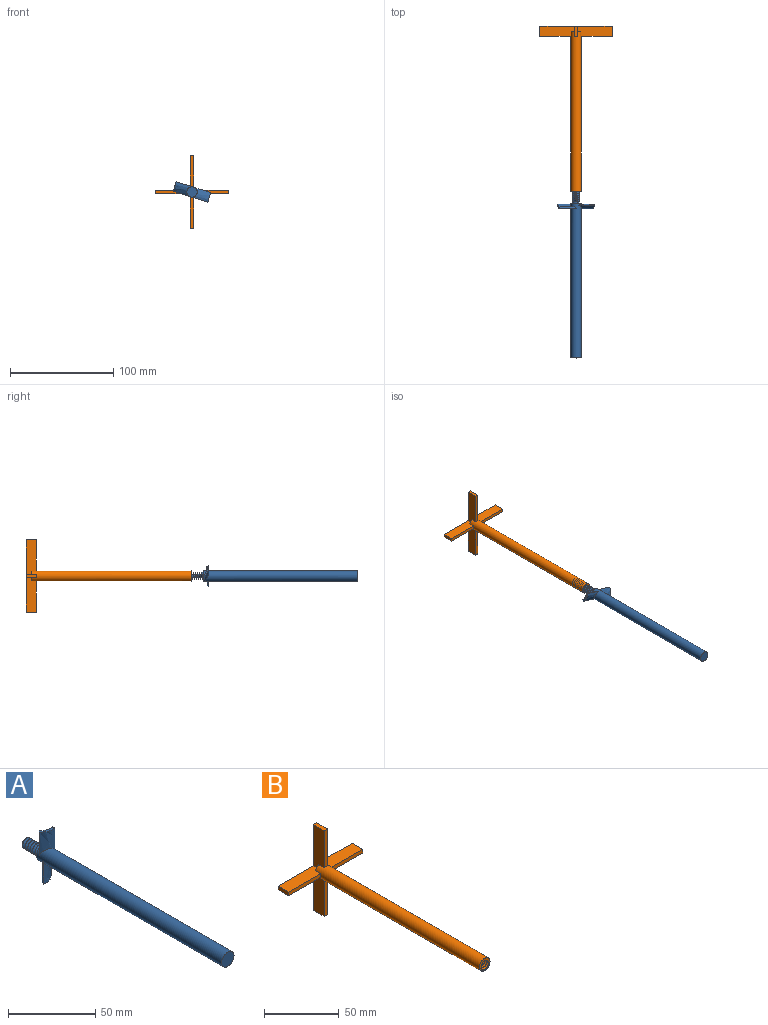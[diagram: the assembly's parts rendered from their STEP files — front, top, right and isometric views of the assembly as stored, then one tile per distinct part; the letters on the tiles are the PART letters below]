
ASSEMBLY  parts=2 mates=1
PART A: 21 faces, bbox 10.6x165.8x35.6 mm
  f0: cylinder r=5mm len=150mm, axis (0,1,0), area 4675.9mm2, adj f3,f4,f11,f12,f13,f14,f16,f17
  f1: cylinder r=3.5mm len=13.5mm, axis (0,-1,0), area 58.9mm2, adj f4,f5,f7,f8,f10
  f2: plane 6.3x5.6mm, normal (0,1,0), area 22.2mm2, adj f5,f6,f7,f8
  f3: plane 10x10mm, normal (0,-1,0), area 78.5mm2, adj f0
  f4: plane 10x10mm, normal (0,1,0), area 40.1mm2, adj f0,f1,f9
  f5: cone r=3.5mm half-angle=45deg, axis (0,-1,0), area 3mm2, adj f1,f2,f6,f7,f8
  f6: plane 0.5x0.29mm, normal (0,0,1), area 0mm2, adj f2,f5,f8
  f7: bspline ~14.62x8.08mm, area 205.9mm2, adj f1,f2,f5,f8,f10
  f8: bspline ~14.95x8.08mm, area 225.2mm2, adj f1,f2,f5,f6,f7,f9,f10
  f9: cylinder r=3.5mm len=3.37mm, axis (0,-1,0), area 0.9mm2, adj f4,f8,f10
  f10: plane 1.9x1.65mm, normal (0,0,-1), area 1.6mm2, adj f1,f7,f8,f9
  f11: extruded ~14.51x7.74mm, area 111.1mm2, adj f0,f13,f14,f15
  f12: extruded ~16.13x9.6mm, area 141.5mm2, adj f0,f13,f14,f15
  f13: plane 16.31x1.59mm, normal (-0.86,0.5,0), area 23.7mm2, adj f0,f11,f12,f15
  f14: plane 16.35x1.29mm, normal (0.7,0.71,0), area 22.6mm2, adj f0,f11,f12,f15
  f15: plane 9.6x4.41mm, normal (0,0,-1), area 14.3mm2, adj f11,f12,f13,f14
  f16: extruded ~15.22x8.23mm, area 119mm2, adj f0,f18,f19,f20
  f17: extruded ~16.28x9.6mm, area 141.5mm2, adj f0,f18,f19,f20
  f18: plane 16.5x1.66mm, normal (0.96,0.27,0), area 23.5mm2, adj f0,f16,f17,f20
  f19: plane 16.14x1.34mm, normal (-0.76,0.65,0), area 22.4mm2, adj f0,f16,f17,f20
  f20: plane 9.6x4.48mm, normal (0,0,1), area 14.7mm2, adj f16,f17,f18,f19
PART B: 30 faces, bbox 70.6x161.9x70.6 mm
  f0: plane 10.62x10.62mm, normal (0,-1,0), area 38.4mm2, adj f3,f26,f27,f29
  f1: plane 33.5x10mm, normal (0,0,-1), area 318.7mm2, adj f3,f7,f11,f12,f18,f22
  f2: plane 33.5x10mm, normal (1,0,0), area 318.7mm2, adj f3,f4,f13,f14,f18,f19
  f3: cylinder r=5mm len=155mm, axis (0,1,0), area 4808.5mm2, adj f0,f1,f2,f4,f5,f6,f7,f8
  f4: plane 30.23x3mm, normal (0,-1,0), area 90.2mm2, adj f2,f3,f14,f15
  f5: plane 30.23x3mm, normal (0,-1,0), area 90.2mm2, adj f3,f8,f16,f17
  f6: plane 30.23x3mm, normal (0,-1,0), area 90.2mm2, adj f3,f9,f10,f11
  f7: plane 30.23x3mm, normal (0,-1,0), area 90.2mm2, adj f1,f3,f12,f13
  f8: plane 33.5x10mm, normal (0,0,-1), area 318.7mm2, adj f3,f5,f9,f17,f18,f21
  f9: plane 33.5x10mm, normal (-1,0,0), area 318.7mm2, adj f3,f6,f8,f10,f18,f21
  f10: plane 10x3mm, normal (0,0,-1), area 30mm2, adj f6,f9,f11,f18
  f11: plane 33.5x10mm, normal (1,0,0), area 318.7mm2, adj f1,f3,f6,f10,f18,f22
  f12: plane 10x3mm, normal (1,0,0), area 30mm2, adj f1,f7,f13,f18
  f13: plane 33.5x10mm, normal (0,0,1), area 318.7mm2, adj f2,f3,f7,f12,f18,f19
  f14: plane 10x3mm, normal (0,0,1), area 30mm2, adj f2,f4,f15,f18
  f15: plane 33.5x10mm, normal (-1,0,0), area 318.7mm2, adj f3,f4,f14,f16,f18,f20
  f16: plane 33.5x10mm, normal (0,0,1), area 318.7mm2, adj f3,f5,f15,f17,f18,f20
  f17: plane 10x3mm, normal (-1,0,0), area 30mm2, adj f5,f8,f16,f18
  f18: plane 70x70mm, normal (0,1,0), area 411mm2, adj f1,f2,f8,f9,f10,f11,f12,f13
  f19: plane 3.27x3.27mm, normal (0,1,0), area 7.1mm2, adj f2,f3,f13
  f20: plane 3.27x3.27mm, normal (0,1,0), area 7.1mm2, adj f3,f15,f16
  f21: plane 3.27x3.27mm, normal (0,1,0), area 7.1mm2, adj f3,f8,f9
  f22: plane 3.27x3.27mm, normal (0,1,0), area 7.1mm2, adj f1,f3,f11
  f23: cylinder r=2.67mm len=15mm, axis (0,-1,0), area 53mm2, adj f25,f26,f27,f28,f29
  f24: plane 4.88x4.43mm, normal (0,-1,0), area 15.3mm2, adj f25,f27,f28
  f25: plane 2.15x1.93mm, normal (-1,0,0), area 1.7mm2, adj f23,f24,f26,f27,f28
  f26: bspline ~16.28x9.98mm, area 305.9mm2, adj f0,f23,f25,f27,f29
  f27: bspline ~17.61x9.98mm, area 322.3mm2, adj f0,f23,f24,f25,f26,f28,f29
  f28: cone r=2.17mm half-angle=45deg, axis (0,-1,0), area 8.8mm2, adj f23,f24,f25,f27
  f29: cone r=2.67mm half-angle=45deg, axis (0,-1,0), area 2.6mm2, adj f0,f23,f26,f27
PLACE A rot(axis=(0,-1,0),72.7deg) t=(-124.38,-57.07,-130.33)mm
PLACE B t=(-105.27,104.53,-69.01)mm fixed
MATE cylindrical B.f3 <-> A.f0  axis (0,-1,0) through (-105.27,-45.47,-69.01)mm
